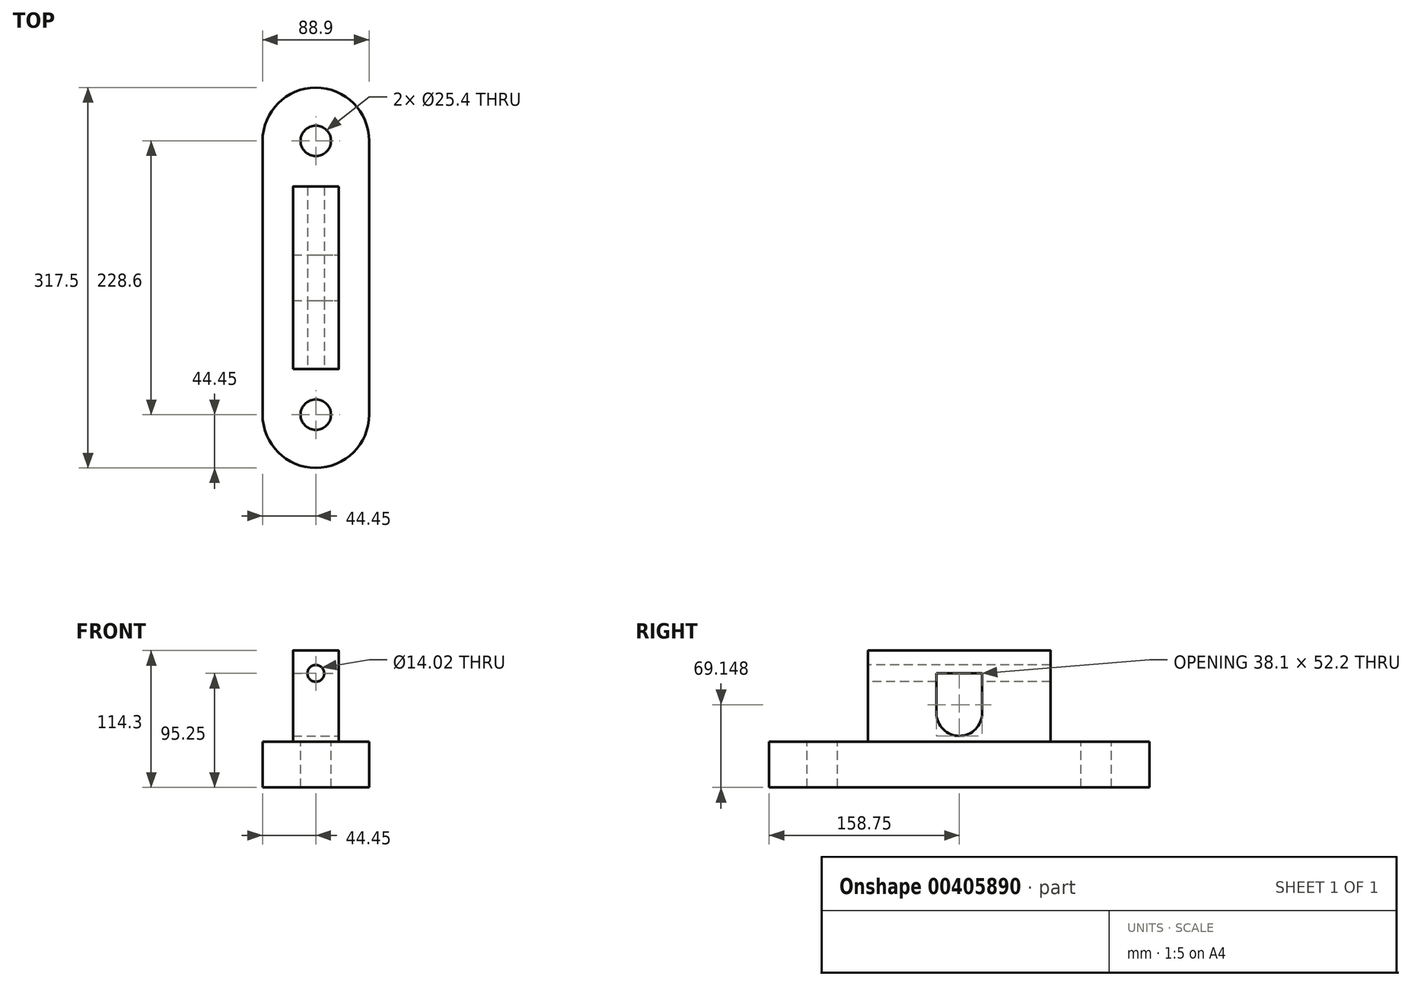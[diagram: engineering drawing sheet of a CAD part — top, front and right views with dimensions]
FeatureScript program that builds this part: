
annotation { "Feature Type Name" : "Feature", "Feature Type Description" : "" }
export const myFeature = defineFeature(function(context is Context, id is Id, definition is map)
    precondition{}
    {
        {
            var Q0;
            Q0=qCreatedBy(makeId("Top.planeOp"),FACE);
            var sketch = newSketch(context, id + "F0", { "sketchPlane" : qUnion([Q0])});
            skLineSegment(sketch, "E0.bottom", {"start": v(-44.45, 114.3) * mm, "end": v(44.45, 114.3) * mm});
            skLineSegment(sketch, "E0.top", {"start": v(-44.45, -114.3) * mm, "end": v(44.45, -114.3) * mm});
            skLineSegment(sketch, "E0.left", {"start": v(-44.45, 114.3) * mm, "end": v(-44.45, -114.3) * mm});
            skLineSegment(sketch, "E0.right", {"start": v(44.45, 114.3) * mm, "end": v(44.45, -114.3) * mm});
            skPoint(sketch, "E0.middle", {"position": v(0, 0) * mm});
            skCircle(sketch, "E1", {"center": v(0, -114.3) * mm, "radius": 44.45 * mm});
            skCircle(sketch, "E2", {"center": v(0, 114.3) * mm, "radius": 44.45 * mm});
            skSolve(sketch);
        }
        {
            var Q0;
            {var subQ0=sQuery(id+"F0.wireOp",EDGE,"E0.bottom");Q0=makeQuery(id+"F0.imprint","IMPRINT",FACE,{"disambiguationData":[TD([[makeQuery(id+"F0.imprint","IMPRINT",EDGE,{"derivedFrom":subQ0}),1.0]])]});}
            var Q1;
            {var subQ0=sQuery(id+"F0.wireOp",EDGE,"E0.bottom");Q1=makeQuery(id+"F0.imprint","IMPRINT",FACE,{"disambiguationData":[TD([[makeQuery(id+"F0.imprint","IMPRINT",EDGE,{"derivedFrom":subQ0}),-1.0]])]});}
            var Q2;
            {var subQ0=sQuery(id+"F0.wireOp",EDGE,"E0.left");Q2=makeQuery(id+"F0.imprint","IMPRINT",FACE,{"disambiguationData":[TD([[makeQuery(id+"F0.imprint","IMPRINT",EDGE,{"derivedFrom":subQ0}),1.0]])]});}
            var Q3;
            {var subQ0=sQuery(id+"F0.wireOp",EDGE,"E0.top");Q3=makeQuery(id+"F0.imprint","IMPRINT",FACE,{"disambiguationData":[TD([[makeQuery(id+"F0.imprint","IMPRINT",EDGE,{"derivedFrom":subQ0}),1.0]])]});}
            var Q4;
            {var subQ0=sQuery(id+"F0.wireOp",EDGE,"E0.top");Q4=makeQuery(id+"F0.imprint","IMPRINT",FACE,{"disambiguationData":[TD([[makeQuery(id+"F0.imprint","IMPRINT",EDGE,{"derivedFrom":subQ0}),-1.0]])]});}
            extrude(context, id + "F1", {"entities" : qUnion([Q0, Q1, Q2, Q3, Q4]), "depth" : 38.1 * mm});
        }
        {
            var Q0;
            Q0=makeQuery(id+"F1.opExtrude","CAP_FACE",FACE,{"disambiguationData":[OSD([sQuery(id+"F0.wireOp",EDGE,"E0.left"),sQuery(id+"F0.wireOp",EDGE,"E0.right"),sQuery(id+"F0.wireOp",EDGE,"E1"),sQuery(id+"F0.wireOp",EDGE,"E2")])],"isStart":false});
            var sketch = newSketch(context, id + "F2", { "sketchPlane" : qUnion([Q0])});
            skCircle(sketch, "E3", {"center": v(0, 114.3) * mm, "radius": 12.7 * mm});
            skCircle(sketch, "E4", {"center": v(0, -114.3) * mm, "radius": 12.7 * mm});
            skSolve(sketch);
        }
        {
            var Q0;
            Q0=makeQuery(id+"F2.imprint","IMPRINT",FACE,{"disambiguationData":[TD([[makeQuery(id+"F2.imprint","IMPRINT",EDGE,{"derivedFrom":sQuery(id+"F2.wireOp",EDGE,"E3")}),1.0]])]});
            var Q1;
            Q1=makeQuery(id+"F2.imprint","IMPRINT",FACE,{"disambiguationData":[TD([[makeQuery(id+"F2.imprint","IMPRINT",EDGE,{"derivedFrom":sQuery(id+"F2.wireOp",EDGE,"E4")}),1.0]])]});
            extrude(context, id + "F3", {"entities" : qUnion([Q0, Q1]), "operationType" : NewBodyOperationType.REMOVE, "endBound" : BoundingType.THROUGH_ALL, "oppositeDirection" : true, "depth" : 25.4 * mm});
        }
        {
            var Q0;
            Q0=makeQuery(id+"F1.opExtrude","CAP_FACE",FACE,{"disambiguationData":[OSD([sQuery(id+"F0.wireOp",EDGE,"E0.left"),sQuery(id+"F0.wireOp",EDGE,"E0.right"),sQuery(id+"F0.wireOp",EDGE,"E1"),sQuery(id+"F0.wireOp",EDGE,"E2")])],"isStart":false});
            var sketch = newSketch(context, id + "F4", { "sketchPlane" : qUnion([Q0])});
            skLineSegment(sketch, "E5.bottom", {"start": v(-19.05, 76.2) * mm, "end": v(19.05, 76.2) * mm});
            skLineSegment(sketch, "E5.top", {"start": v(-19.05, -76.2) * mm, "end": v(19.05, -76.2) * mm});
            skLineSegment(sketch, "E5.left", {"start": v(-19.05, 76.2) * mm, "end": v(-19.05, -76.2) * mm});
            skLineSegment(sketch, "E5.right", {"start": v(19.05, 76.2) * mm, "end": v(19.05, -76.2) * mm});
            skPoint(sketch, "E5.middle", {"position": v(0, 0) * mm});
            skSolve(sketch);
        }
        {
            var Q0;
            Q0=makeQuery(id+"F4.imprint","IMPRINT",FACE,{"disambiguationData":[TD([[makeQuery(id+"F4.imprint","IMPRINT",EDGE,{"derivedFrom":sQuery(id+"F4.wireOp",EDGE,"E5.bottom")}),-1.0]])]});
            extrude(context, id + "F5", {"entities" : qUnion([Q0]), "operationType" : NewBodyOperationType.ADD, "depth" : 76.2 * mm});
        }
        {
            var Q0;
            Q0=makeQuery(id+"F5.opExtrude","CAP_EDGE",EDGE,{"disambiguationData":[OSD([sQuery(id+"F4.wireOp",EDGE,"E5.right")])],"isStart":false});
            var Q1;
            Q1=makeQuery(id+"F5.opExtrude","CAP_EDGE",EDGE,{"disambiguationData":[OSD([sQuery(id+"F4.wireOp",EDGE,"E5.left")])],"isStart":false});
            fillet(context, id + "F6", {"entities" : qUnion([Q0, Q1]), "radius" : 1.5 / 50.8 * mm, "tangentPropagation" : true, "allowEdgeOverflow" : false});
        }
        {
            var Q0;
            Q0=makeQuery(id+"F5.opExtrude","SWEPT_FACE",FACE,{"disambiguationData":[OSD([sQuery(id+"F4.wireOp",EDGE,"E5.top")])]});
            var sketch = newSketch(context, id + "F7", { "sketchPlane" : qUnion([Q0])});
            skCircle(sketch, "E6", {"center": v(0, 95.25) * mm, "radius": 7.01 * mm});
            skSolve(sketch);
        }
        {
            var Q0;
            Q0=makeQuery(id+"F7.imprint","IMPRINT",FACE,{"disambiguationData":[TD([[makeQuery(id+"F7.imprint","IMPRINT",EDGE,{"derivedFrom":sQuery(id+"F7.wireOp",EDGE,"E6")}),1.0]])]});
            extrude(context, id + "F8", {"entities" : qUnion([Q0]), "operationType" : NewBodyOperationType.REMOVE, "endBound" : BoundingType.THROUGH_ALL, "oppositeDirection" : true, "depth" : 25.4 * mm});
        }
        {
            var Q0;
            Q0=makeQuery(id+"F5.opExtrude","SWEPT_FACE",FACE,{"disambiguationData":[OSD([sQuery(id+"F4.wireOp",EDGE,"E5.right")])]});
            var sketch = newSketch(context, id + "F9", { "sketchPlane" : qUnion([Q0])});
            skLineSegment(sketch, "E7", {"start": v(-101.6, 114.3) * mm, "end": v(101.6, 114.3) * mm});
            skLineSegment(sketch, "E8.0.0", {"start": v(76.2, 38.1) * mm, "end": v(76.2, 95.25) * mm});
            skLineSegment(sketch, "E8.0.1", {"start": v(76.2, 95.25) * mm, "end": v(-76.2, 95.25) * mm});
            skLineSegment(sketch, "E8.0.2", {"start": v(-76.2, 95.25) * mm, "end": v(-76.2, 38.1) * mm});
            skLineSegment(sketch, "E8.0.3", {"start": v(-76.2, 38.1) * mm, "end": v(76.2, 38.1) * mm});
            skLineSegment(sketch, "E9.bottom", {"start": v(-19.05, 114.3) * mm, "end": v(19.05, 114.3) * mm});
            skLineSegment(sketch, "E9.top", {"start": v(-19.05, 62.1) * mm, "end": v(19.05, 62.1) * mm});
            skLineSegment(sketch, "E9.left", {"start": v(-19.05, 114.3) * mm, "end": v(-19.05, 62.1) * mm});
            skLineSegment(sketch, "E9.right", {"start": v(19.05, 114.3) * mm, "end": v(19.05, 62.1) * mm});
            skPoint(sketch, "E10", {"position": v(0, 62.1) * mm});
            skCircle(sketch, "E11", {"center": v(0, 62.1) * mm, "radius": 19.05 * mm});
            skSolve(sketch);
        }
        {
            var Q0;
            {var subQ0=sQuery(id+"F9.wireOp",EDGE,"E9.top");Q0=makeQuery(id+"F9.imprint","IMPRINT",FACE,{"disambiguationData":[TD([[makeQuery(id+"F9.imprint","IMPRINT",EDGE,{"derivedFrom":subQ0}),-1.0]])]});}
            var Q1;
            {var subQ0=sQuery(id+"F9.wireOp",EDGE,"E9.top");Q1=makeQuery(id+"F9.imprint","IMPRINT",FACE,{"disambiguationData":[TD([[makeQuery(id+"F9.imprint","IMPRINT",EDGE,{"derivedFrom":subQ0}),1.0]])]});}
            var Q2;
            {var subQ5=sQuery(id+"F9.wireOp",EDGE,"E9.bottom");Q2=makeQuery(id+"F9.imprint","IMPRINT",FACE,{"disambiguationData":[TD([[makeQuery(id+"F9.imprint","IMPRINT",EDGE,{"derivedFrom":subQ5}),-1.0]])]});}
            var Q3;
            {var subQ0=sQuery(id+"F9.wireOp",EDGE,"E9.right");var subQ1=sQuery(id+"F9.wireOp",EDGE,"E8.0.1");var subQ2=makeQuery(id+"F9.imprint","INTERSECT",VERTEX,{"derivedFrom":[subQ1,subQ0]});Q3=makeQuery(id+"F9.imprint","IMPRINT",FACE,{"disambiguationData":[TD([[makeQuery(id+"F9.imprint","IMPRINT",EDGE,{"disambiguationData":[TD([[subQ2,-1.0]])],"derivedFrom":subQ1}),1.0]])]});}
            extrude(context, id + "F10", {"entities" : qUnion([Q0, Q1, Q2, Q3]), "operationType" : NewBodyOperationType.REMOVE, "endBound" : BoundingType.THROUGH_ALL, "oppositeDirection" : true, "depth" : 25.4 * mm});
        }
        {
            var Q0;
            {var subQ0=sQuery(id+"F9.wireOp",EDGE,"E9.top");Q0=makeQuery(id+"F9.imprint","IMPRINT",FACE,{"disambiguationData":[TD([[makeQuery(id+"F9.imprint","IMPRINT",EDGE,{"derivedFrom":subQ0}),-1.0]])]});}
            var Q1;
            {var subQ0=sQuery(id+"F9.wireOp",EDGE,"E9.top");Q1=makeQuery(id+"F9.imprint","IMPRINT",FACE,{"disambiguationData":[TD([[makeQuery(id+"F9.imprint","IMPRINT",EDGE,{"derivedFrom":subQ0}),1.0]])]});}
            var Q2;
            {var subQ5=sQuery(id+"F9.wireOp",EDGE,"E9.bottom");Q2=makeQuery(id+"F9.imprint","IMPRINT",FACE,{"disambiguationData":[TD([[makeQuery(id+"F9.imprint","IMPRINT",EDGE,{"derivedFrom":subQ5}),-1.0]])]});}
            var Q3;
            {var subQ0=sQuery(id+"F9.wireOp",EDGE,"E9.right");var subQ1=sQuery(id+"F9.wireOp",EDGE,"E8.0.1");var subQ2=makeQuery(id+"F9.imprint","INTERSECT",VERTEX,{"derivedFrom":[subQ1,subQ0]});Q3=makeQuery(id+"F9.imprint","IMPRINT",FACE,{"disambiguationData":[TD([[makeQuery(id+"F9.imprint","IMPRINT",EDGE,{"disambiguationData":[TD([[subQ2,-1.0]])],"derivedFrom":subQ1}),1.0]])]});}
            extrude(context, id + "F11", {"entities" : qUnion([Q0, Q1, Q2, Q3]), "operationType" : NewBodyOperationType.REMOVE, "oppositeDirection" : true, "depth" : 25.4 * mm});
        }
    });
